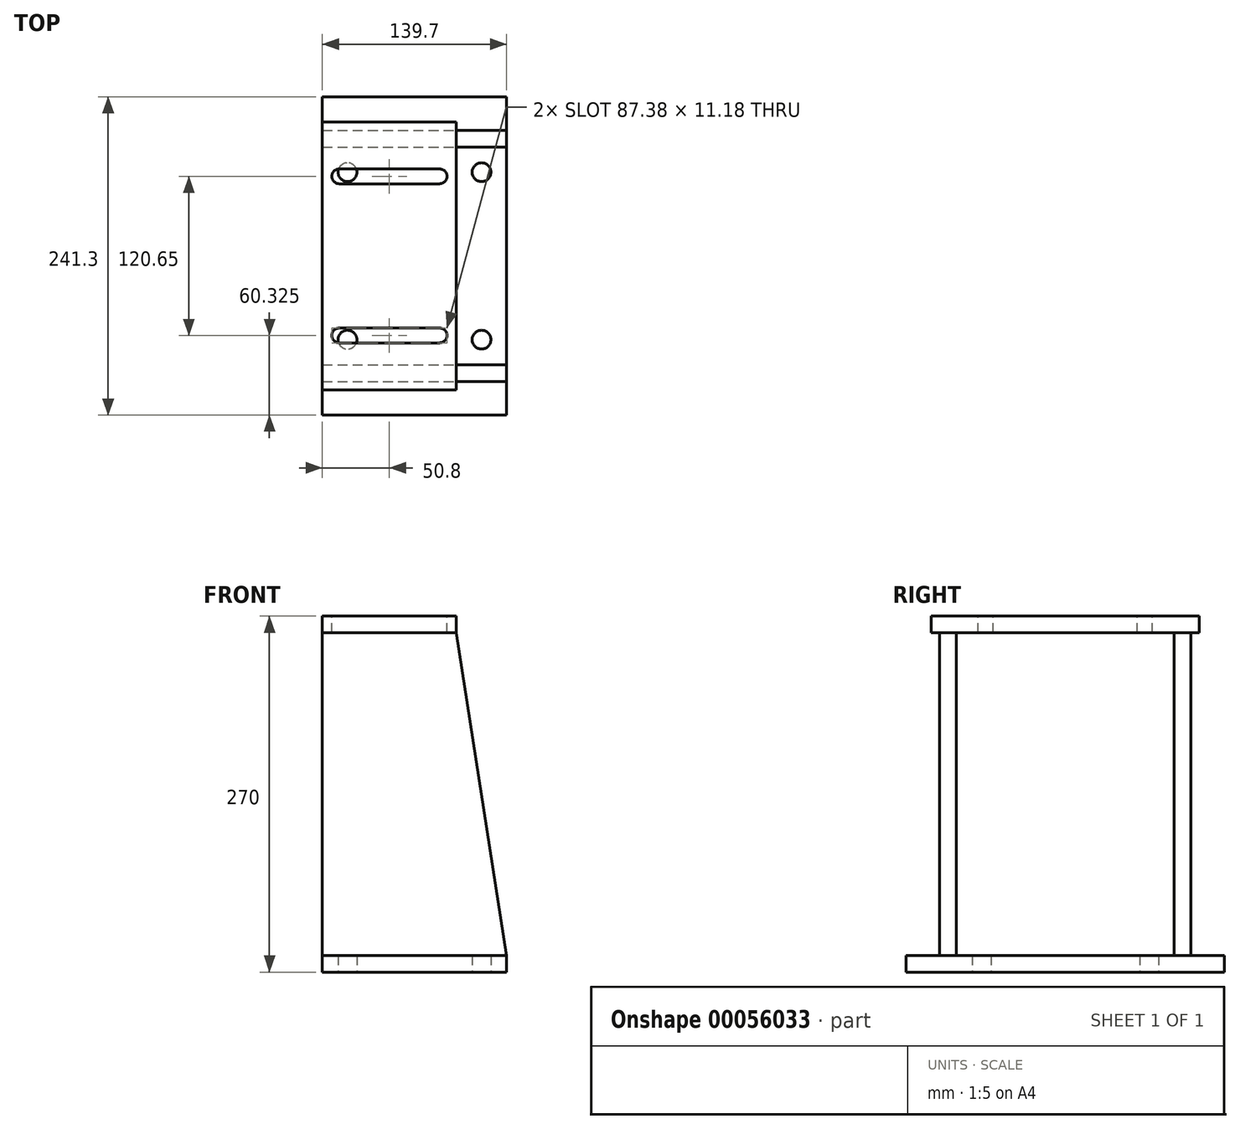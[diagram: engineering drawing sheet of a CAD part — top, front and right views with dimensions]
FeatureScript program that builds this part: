
annotation { "Feature Type Name" : "Feature", "Feature Type Description" : "" }
export const myFeature = defineFeature(function(context is Context, id is Id, definition is map)
    precondition{}
    {
        {
            var Q0;
            Q0=qCreatedBy(makeId("Top.planeOp"),FACE);
            var sketch = newSketch(context, id + "F0", { "sketchPlane" : qUnion([Q0])});
            skLineSegment(sketch, "E0.rect.bottom", {"start": v(-69.85, 120.65) * mm, "end": v(69.85, 120.65) * mm});
            skLineSegment(sketch, "E0.rect.top", {"start": v(-69.85, -120.65) * mm, "end": v(69.85, -120.65) * mm});
            skLineSegment(sketch, "E0.rect.left", {"start": v(-69.85, 120.65) * mm, "end": v(-69.85, -120.65) * mm});
            skLineSegment(sketch, "E0.rect.right", {"start": v(69.85, 120.65) * mm, "end": v(69.85, -120.65) * mm});
            skPoint(sketch, "E0.rect.middle", {"position": v(0, 0) * mm});
            skLineSegment(sketch, "E1", {"start": v(0, 120.65) * mm, "end": v(0, -120.65) * mm, "construction": true});
            skLineSegment(sketch, "E2", {"start": v(-69.85, 0) * mm, "end": v(69.85, 0) * mm, "construction": true});
            skLineSegment(sketch, "E3.0", {"start": v(-69.85, 63.5) * mm, "end": v(69.85, 63.5) * mm, "construction": true});
            skLineSegment(sketch, "E4.0", {"start": v(-50.8, 120.65) * mm, "end": v(-50.8, -120.65) * mm, "construction": true});
            skCircle(sketch, "E5", {"center": v(-50.8, 63.5) * mm, "radius": 7.14 * mm});
            skCircle(sketch, "E6.MirrorC", {"center": v(50.8, 63.5) * mm, "radius": 7.14 * mm});
            skCircle(sketch, "E7.MirrorC", {"center": v(-50.8, -63.5) * mm, "radius": 7.14 * mm});
            skCircle(sketch, "E8.MirrorC", {"center": v(50.8, -63.5) * mm, "radius": 7.14 * mm});
            skSolve(sketch);
        }
        {
            var Q0;
            Q0=qSketchRegion(id+"F0",true);
            extrude(context, id + "F1", {"entities" : qUnion([Q0]), "depth" : 12.7 * mm});
        }
        {
            var Q0;
            Q0=qCreatedBy(makeId("Top.planeOp"),FACE);
            cPlane(context, id + "F2", {"entities" : qUnion([Q0]), "cplaneType" : CPlaneType.OFFSET, "offset" : 270 * mm, "width" : 152.4 * mm, "height" : 152.4 * mm});
        }
        {
            var Q0;
            Q0=qCreatedBy(id+"F2.planeOp",FACE);
            var sketch = newSketch(context, id + "F3", { "sketchPlane" : qUnion([Q0])});
            skLineSegment(sketch, "E9.0", {"start": v(-69.85, 120.65) * mm, "end": v(-69.85, -120.65) * mm, "construction": true});
            skLineSegment(sketch, "E10", {"start": v(-85.57, 0) * mm, "end": v(91.78, 0) * mm, "construction": true});
            skLineSegment(sketch, "E11.bottom", {"start": v(-69.85, 101.6) * mm, "end": v(31.75, 101.6) * mm});
            skLineSegment(sketch, "E11.top", {"start": v(-69.85, -101.6) * mm, "end": v(31.75, -101.6) * mm});
            skLineSegment(sketch, "E11.left", {"start": v(-69.85, 101.6) * mm, "end": v(-69.85, -101.6) * mm});
            skLineSegment(sketch, "E11.right", {"start": v(31.75, 101.6) * mm, "end": v(31.75, -101.6) * mm});
            skLineSegment(sketch, "E12.0", {"start": v(-85.57, 60.33) * mm, "end": v(91.78, 60.33) * mm, "construction": true});
            skLineSegment(sketch, "E13", {"start": v(-19.05, 101.6) * mm, "end": v(-19.05, -101.6) * mm, "construction": true});
            skLineSegment(sketch, "E14.0", {"start": v(-57.15, 101.6) * mm, "end": v(-57.15, -101.6) * mm, "construction": true});
            skLineSegment(sketch, "E15.MirrorCS", {"start": v(19.05, 101.6) * mm, "end": v(19.05, -101.6) * mm, "construction": true});
            skLineSegment(sketch, "E16", {"start": v(-57.15, 60.33) * mm, "end": v(19.05, 60.33) * mm});
            skArc(sketch, "E17.0.startCap", {"start": v(-57.15, 54.74) * mm, "mid": v(-62.74, 60.33) * mm, "end": v(-57.15, 65.91) * mm});
            skArc(sketch, "E17.0.endCap", {"start": v(19.05, 65.91) * mm, "mid": v(24.64, 60.33) * mm, "end": v(19.05, 54.74) * mm});
            skLineSegment(sketch, "E17.0.left", {"start": v(-57.15, 65.91) * mm, "end": v(19.05, 65.91) * mm});
            skLineSegment(sketch, "E17.0.right", {"start": v(-57.15, 54.74) * mm, "end": v(19.05, 54.74) * mm});
            skLineSegment(sketch, "E18.MirrorCS", {"start": v(-57.15, -54.74) * mm, "end": v(19.05, -54.74) * mm});
            skLineSegment(sketch, "E19.MirrorCS", {"start": v(-57.15, -65.91) * mm, "end": v(19.05, -65.91) * mm});
            skArc(sketch, "E20.MirrorCS", {"start": v(19.05, -65.91) * mm, "mid": v(24.64, -60.33) * mm, "end": v(19.05, -54.74) * mm});
            skArc(sketch, "E21.MirrorCS", {"start": v(-57.15, -54.74) * mm, "mid": v(-62.74, -60.33) * mm, "end": v(-57.15, -65.91) * mm});
            skLineSegment(sketch, "E22.MirrorCS", {"start": v(-57.15, -60.33) * mm, "end": v(19.05, -60.33) * mm});
            skSolve(sketch);
        }
        {
            var Q0;
            Q0=qSketchRegion(id+"F3",true);
            extrude(context, id + "F4", {"entities" : qUnion([Q0]), "oppositeDirection" : true, "depth" : 12.7 * mm});
        }
        {
            var Q0;
            Q0=makeQuery(id+"F1.opExtrude","CAP_FACE",FACE,{"disambiguationData":[OSD([sQuery(id+"F0.wireOp",EDGE,"E0.rect.bottom"),sQuery(id+"F0.wireOp",EDGE,"E0.rect.top"),sQuery(id+"F0.wireOp",EDGE,"E0.rect.left"),sQuery(id+"F0.wireOp",EDGE,"E0.rect.right"),sQuery(id+"F0.wireOp",EDGE,"E5"),sQuery(id+"F0.wireOp",EDGE,"E6.MirrorC"),sQuery(id+"F0.wireOp",EDGE,"E7.MirrorC"),sQuery(id+"F0.wireOp",EDGE,"E8.MirrorC")])],"isStart":false});
            var sketch = newSketch(context, id + "F5", { "sketchPlane" : qUnion([Q0])});
            skLineSegment(sketch, "E23.0", {"start": v(-69.85, 95.25) * mm, "end": v(69.85, 95.25) * mm});
            skLineSegment(sketch, "E24.0", {"start": v(-69.85, 82.55) * mm, "end": v(69.85, 82.55) * mm});
            skLineSegment(sketch, "E25.0", {"start": v(69.85, 95.25) * mm, "end": v(69.85, 82.55) * mm});
            skLineSegment(sketch, "E26.0", {"start": v(-69.85, 95.25) * mm, "end": v(-69.85, 82.55) * mm});
            skPoint(sketch, "E27.orphan", {"position": v(-69.85, 120.65) * mm});
            skPoint(sketch, "E28.orphan", {"position": v(-69.85, -120.65) * mm});
            skPoint(sketch, "E29.orphan", {"position": v(69.85, 120.65) * mm});
            skPoint(sketch, "E30.orphan", {"position": v(69.85, -120.65) * mm});
            skLineSegment(sketch, "E31", {"start": v(-90.75, 0) * mm, "end": v(99.61, 0) * mm, "construction": true});
            skPoint(sketch, "E31.endSnap0", {"position": v(69.85, 0) * mm});
            skLineSegment(sketch, "E32.MirrorCS", {"start": v(-69.85, -95.25) * mm, "end": v(-69.85, -82.55) * mm});
            skLineSegment(sketch, "E33.MirrorCS", {"start": v(69.85, -95.25) * mm, "end": v(69.85, -82.55) * mm});
            skLineSegment(sketch, "E34.MirrorCS", {"start": v(-69.85, -95.25) * mm, "end": v(69.85, -95.25) * mm});
            skLineSegment(sketch, "E35.MirrorCS", {"start": v(-69.85, -82.55) * mm, "end": v(69.85, -82.55) * mm});
            skSolve(sketch);
        }
        {
            var Q0;
            Q0=qSketchRegion(id+"F5",true);
            var Q1;
            Q1=makeQuery(id+"F4.opExtrude","CAP_FACE",FACE,{"disambiguationData":[OSD([sQuery(id+"F3.wireOp",EDGE,"E11.bottom"),sQuery(id+"F3.wireOp",EDGE,"E11.top"),sQuery(id+"F3.wireOp",EDGE,"E11.left"),sQuery(id+"F3.wireOp",EDGE,"E11.right"),sQuery(id+"F3.wireOp",EDGE,"E17.0.startCap"),sQuery(id+"F3.wireOp",EDGE,"E17.0.endCap"),sQuery(id+"F3.wireOp",EDGE,"E17.0.left"),sQuery(id+"F3.wireOp",EDGE,"E17.0.right"),sQuery(id+"F3.wireOp",EDGE,"E18.MirrorCS"),sQuery(id+"F3.wireOp",EDGE,"E19.MirrorCS"),sQuery(id+"F3.wireOp",EDGE,"E20.MirrorCS"),sQuery(id+"F3.wireOp",EDGE,"E21.MirrorCS")])],"isStart":false});
            extrude(context, id + "F6", {"entities" : qUnion([Q0]), "endBound" : BoundingType.UP_TO_SURFACE, "endBoundEntityFace" : qUnion([Q1]), "depth" : 25.4 * mm});
        }
        {
            var Q0;
            Q0=makeQuery(id+"F1.opExtrude","SWEPT_BODY",BODY,{"disambiguationData":[OSD([sQuery(id+"F0.wireOp",EDGE,"E0.rect.bottom"),sQuery(id+"F0.wireOp",EDGE,"E0.rect.top"),sQuery(id+"F0.wireOp",EDGE,"E0.rect.left"),sQuery(id+"F0.wireOp",EDGE,"E0.rect.right"),sQuery(id+"F0.wireOp",EDGE,"E5"),sQuery(id+"F0.wireOp",EDGE,"E6.MirrorC"),sQuery(id+"F0.wireOp",EDGE,"E7.MirrorC"),sQuery(id+"F0.wireOp",EDGE,"E8.MirrorC")])]});
            var Q1;
            Q1=makeQuery(id+"F6.opExtrude","SWEPT_BODY",BODY,{"disambiguationData":[OSD([sQuery(id+"F5.wireOp",EDGE,"E32.MirrorCS"),sQuery(id+"F5.wireOp",EDGE,"E33.MirrorCS"),sQuery(id+"F5.wireOp",EDGE,"E34.MirrorCS"),sQuery(id+"F5.wireOp",EDGE,"E35.MirrorCS")])]});
            var Q2;
            Q2=makeQuery(id+"F6.opExtrude","SWEPT_BODY",BODY,{"disambiguationData":[OSD([sQuery(id+"F5.wireOp",EDGE,"E23.0"),sQuery(id+"F5.wireOp",EDGE,"E24.0"),sQuery(id+"F5.wireOp",EDGE,"E25.0"),sQuery(id+"F5.wireOp",EDGE,"E26.0")])]});
            var Q3;
            Q3=makeQuery(id+"F4.opExtrude","SWEPT_BODY",BODY,{"disambiguationData":[OSD([sQuery(id+"F3.wireOp",EDGE,"E11.bottom"),sQuery(id+"F3.wireOp",EDGE,"E11.top"),sQuery(id+"F3.wireOp",EDGE,"E11.left"),sQuery(id+"F3.wireOp",EDGE,"E11.right"),sQuery(id+"F3.wireOp",EDGE,"E17.0.startCap"),sQuery(id+"F3.wireOp",EDGE,"E17.0.endCap"),sQuery(id+"F3.wireOp",EDGE,"E17.0.left"),sQuery(id+"F3.wireOp",EDGE,"E17.0.right"),sQuery(id+"F3.wireOp",EDGE,"E18.MirrorCS"),sQuery(id+"F3.wireOp",EDGE,"E19.MirrorCS"),sQuery(id+"F3.wireOp",EDGE,"E20.MirrorCS"),sQuery(id+"F3.wireOp",EDGE,"E21.MirrorCS")])]});
            booleanBodies(context, id + "F7", {"operationType" : BooleanOperationType.UNION, "tools" : qUnion([Q0, Q1, Q2, Q3])});
        }
        {
            var Q0;
            Q0=makeQuery(id+"F6.opExtrude","SWEPT_FACE",FACE,{"disambiguationData":[OSD([sQuery(id+"F5.wireOp",EDGE,"E34.MirrorCS")])]});
            var sketch = newSketch(context, id + "F8", { "sketchPlane" : qUnion([Q0])});
            skLineSegment(sketch, "E36.0", {"start": v(-69.85, 257.3) * mm, "end": v(31.75, 257.3) * mm, "construction": true});
            skLineSegment(sketch, "E37.0", {"start": v(31.75, 257.3) * mm, "end": v(31.75, 270) * mm, "construction": true});
            skLineSegment(sketch, "E38.0", {"start": v(-69.85, 12.7) * mm, "end": v(69.85, 12.7) * mm, "construction": true});
            skLineSegment(sketch, "E39.bottom", {"start": v(31.75, 257.3) * mm, "end": v(69.85, 257.3) * mm});
            skLineSegment(sketch, "E39.right", {"start": v(69.85, 257.3) * mm, "end": v(69.85, 12.7) * mm});
            skLineSegment(sketch, "E40", {"start": v(31.75, 257.3) * mm, "end": v(69.85, 12.7) * mm});
            skSolve(sketch);
        }
        {
            var Q0;
            Q0=qSketchRegion(id+"F8",true);
            extrude(context, id + "F9", {"entities" : qUnion([Q0]), "operationType" : NewBodyOperationType.REMOVE, "endBound" : BoundingType.THROUGH_ALL, "oppositeDirection" : true, "depth" : 25.4 * mm});
        }
    });
